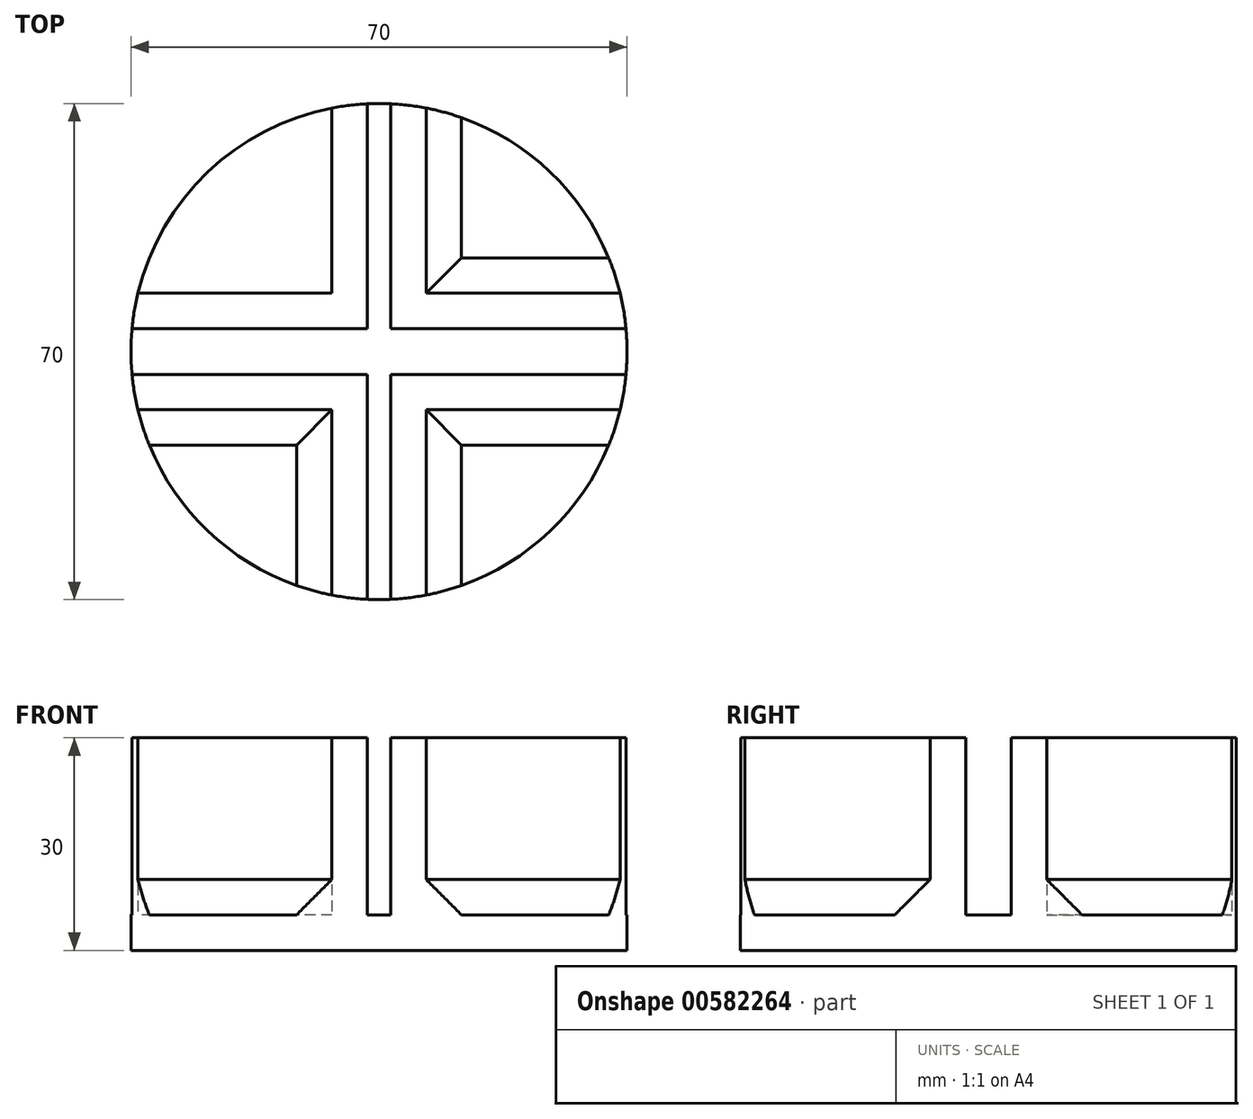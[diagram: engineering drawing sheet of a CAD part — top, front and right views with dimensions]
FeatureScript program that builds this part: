
annotation { "Feature Type Name" : "Feature", "Feature Type Description" : "" }
export const myFeature = defineFeature(function(context is Context, id is Id, definition is map)
    precondition{}
    {
        {
            var Q0;
            Q0=qCreatedBy(makeId("Top.planeOp"),FACE);
            var sketch = newSketch(context, id + "F0", { "sketchPlane" : qUnion([Q0])});
            skCircle(sketch, "E0", {"center": v(0, 0) * mm, "radius": 35 * mm});
            skSolve(sketch);
        }
        {
            var Q0;
            Q0 = qSketchRegion(id + "F0", true);
            extrude(context, id + "F1", {"entities" : qUnion([Q0]), "oppositeDirection" : true, "depth" : 5 * mm, "offsetDistance" : 25 * mm});
        }
        {
            var Q0;
            Q0=makeQuery(id+"F1.opExtrude","CAP_FACE",FACE,{"disambiguationData":[OSD([sQuery(id+"F0.wireOp",EDGE,"E0")])],"isStart":true});
            var sketch = newSketch(context, id + "F2", { "sketchPlane" : qUnion([Q0])});
            skArc(sketch, "E1.0", {"start": v(-34.02, 8.22) * mm, "mid": v(-34.53, 5.74) * mm, "end": v(-34.85, 3.23) * mm});
            skLineSegment(sketch, "E2.bottom", {"start": v(1.65, 39.43) * mm, "end": v(-1.65, 39.43) * mm, "construction": true});
            skLineSegment(sketch, "E2.top", {"start": v(1.65, -39.43) * mm, "end": v(-1.65, -39.43) * mm, "construction": true});
            skLineSegment(sketch, "E2.left", {"start": v(1.65, 39.43) * mm, "end": v(1.65, -39.43) * mm, "construction": true});
            skLineSegment(sketch, "E2.right", {"start": v(-1.65, 39.43) * mm, "end": v(-1.65, -39.43) * mm, "construction": true});
            skLineSegment(sketch, "E3.bottom", {"start": v(44.55, 3.23) * mm, "end": v(-44.55, 3.23) * mm, "construction": true});
            skLineSegment(sketch, "E3.top", {"start": v(44.55, -3.23) * mm, "end": v(-44.55, -3.23) * mm, "construction": true});
            skLineSegment(sketch, "E3.left", {"start": v(44.55, 3.23) * mm, "end": v(44.55, -3.23) * mm, "construction": true});
            skLineSegment(sketch, "E3.right", {"start": v(-44.55, 3.23) * mm, "end": v(-44.55, -3.23) * mm, "construction": true});
            skLineSegment(sketch, "E4", {"start": v(-1.65, 34.96) * mm, "end": v(-1.65, 3.23) * mm});
            skLineSegment(sketch, "E5", {"start": v(-1.65, 3.23) * mm, "end": v(-34.85, 3.23) * mm});
            skLineSegment(sketch, "E6", {"start": v(-34.85, -3.23) * mm, "end": v(-1.65, -3.23) * mm});
            skLineSegment(sketch, "E7", {"start": v(-1.65, -3.23) * mm, "end": v(-1.65, -34.96) * mm});
            skLineSegment(sketch, "E8", {"start": v(1.65, -35.12) * mm, "end": v(1.65, -3.23) * mm});
            skLineSegment(sketch, "E9", {"start": v(1.65, -3.23) * mm, "end": v(34.85, -3.23) * mm});
            skLineSegment(sketch, "E10", {"start": v(34.85, -3.23) * mm, "end": v(35.45, 3.23) * mm});
            skLineSegment(sketch, "E11", {"start": v(35.45, 3.23) * mm, "end": v(1.65, 3.23) * mm});
            skLineSegment(sketch, "E12", {"start": v(1.65, 3.23) * mm, "end": v(1.65, 34.96) * mm});
            skLineSegment(sketch, "E13.0", {"start": v(44.55, 8.23) * mm, "end": v(34.02, 8.23) * mm, "construction": true});
            skLineSegment(sketch, "E14", {"start": v(-6.65, 8.23) * mm, "end": v(-6.65, 34.36) * mm});
            skLineSegment(sketch, "E15.trimOffspring", {"start": v(-6.65, -34.36) * mm, "end": v(-6.65, -39.43) * mm, "construction": true});
            skLineSegment(sketch, "E16.trimOffspring", {"start": v(-6.65, 8.23) * mm, "end": v(-34.02, 8.23) * mm});
            skLineSegment(sketch, "E17.MirrorCS", {"start": v(6.65, 8.23) * mm, "end": v(6.65, 34.36) * mm});
            skLineSegment(sketch, "E18.MirrorCS", {"start": v(6.65, 8.23) * mm, "end": v(34.02, 8.23) * mm});
            skLineSegment(sketch, "E19.MirrorCS", {"start": v(6.65, -8.23) * mm, "end": v(34.02, -8.23) * mm});
            skLineSegment(sketch, "E20.MirrorCS", {"start": v(6.65, -8.23) * mm, "end": v(6.65, -34.36) * mm});
            skLineSegment(sketch, "E21.MirrorCS", {"start": v(-6.65, -8.23) * mm, "end": v(-6.65, -34.36) * mm});
            skLineSegment(sketch, "E22.MirrorCS", {"start": v(-6.65, -8.23) * mm, "end": v(-34.02, -8.23) * mm});
            skArc(sketch, "E23.trimOffspring", {"start": v(-1.65, 34.96) * mm, "mid": v(-4.16, 34.75) * mm, "end": v(-6.65, 34.36) * mm});
            skArc(sketch, "E24.trimOffspring", {"start": v(6.65, 34.36) * mm, "mid": v(4.16, 34.75) * mm, "end": v(1.65, 34.96) * mm});
            skArc(sketch, "E25.trimOffspring", {"start": v(34.85, 3.22) * mm, "mid": v(34.53, 5.74) * mm, "end": v(34.02, 8.23) * mm});
            skArc(sketch, "E26.trimOffspring", {"start": v(34.02, -8.23) * mm, "mid": v(34.53, -5.74) * mm, "end": v(34.85, -3.23) * mm});
            skArc(sketch, "E27.trimOffspring", {"start": v(-6.65, -34.36) * mm, "mid": v(0, -35) * mm, "end": v(6.65, -34.36) * mm});
            skArc(sketch, "E28.trimOffspring", {"start": v(-34.85, -3.23) * mm, "mid": v(-34.53, -5.74) * mm, "end": v(-34.02, -8.23) * mm});
            skSolve(sketch);
        }
        {
            var Q0;
            Q0 = qSketchRegion(id + "F2", true);
            extrude(context, id + "F3", {"entities" : qUnion([Q0]), "operationType" : NewBodyOperationType.ADD, "depth" : 25 * mm, "offsetDistance" : 25 * mm});
        }
        {
            var Q0;
            Q0=makeQuery(id+"F3.opExtrude","CAP_EDGE",EDGE,{"disambiguationData":[OSD([sQuery(id+"F2.wireOp",EDGE,"E14")])],"isStart":true});
            var Q1;
            Q1=makeQuery(id+"F3.opExtrude","CAP_EDGE",EDGE,{"disambiguationData":[OSD([sQuery(id+"F2.wireOp",EDGE,"E16.trimOffspring")])],"isStart":true});
            var Q2;
            Q2=makeQuery(id+"F3.opExtrude","CAP_EDGE",EDGE,{"disambiguationData":[OSD([sQuery(id+"F2.wireOp",EDGE,"E22.MirrorCS")])],"isStart":true});
            var Q3;
            Q3=makeQuery(id+"F3.opExtrude","CAP_EDGE",EDGE,{"disambiguationData":[OSD([sQuery(id+"F2.wireOp",EDGE,"E21.MirrorCS")])],"isStart":true});
            var Q4;
            Q4=makeQuery(id+"F3.opExtrude","CAP_EDGE",EDGE,{"disambiguationData":[OSD([sQuery(id+"F2.wireOp",EDGE,"E20.MirrorCS")])],"isStart":true});
            var Q5;
            Q5=makeQuery(id+"F3.opExtrude","CAP_EDGE",EDGE,{"disambiguationData":[OSD([sQuery(id+"F2.wireOp",EDGE,"E19.MirrorCS")])],"isStart":true});
            var Q6;
            Q6=makeQuery(id+"F3.opExtrude","CAP_EDGE",EDGE,{"disambiguationData":[OSD([sQuery(id+"F2.wireOp",EDGE,"E17.MirrorCS")])],"isStart":true});
            var Q7;
            Q7=makeQuery(id+"F3.opExtrude","CAP_EDGE",EDGE,{"disambiguationData":[OSD([sQuery(id+"F2.wireOp",EDGE,"E18.MirrorCS")])],"isStart":true});
            chamfer(context, id + "F4", {"entities" : qUnion([Q0, Q1, Q2, Q3, Q4, Q5, Q6, Q7]), "width" : 5 * mm, "tangentPropagation" : true});
        }
    });
